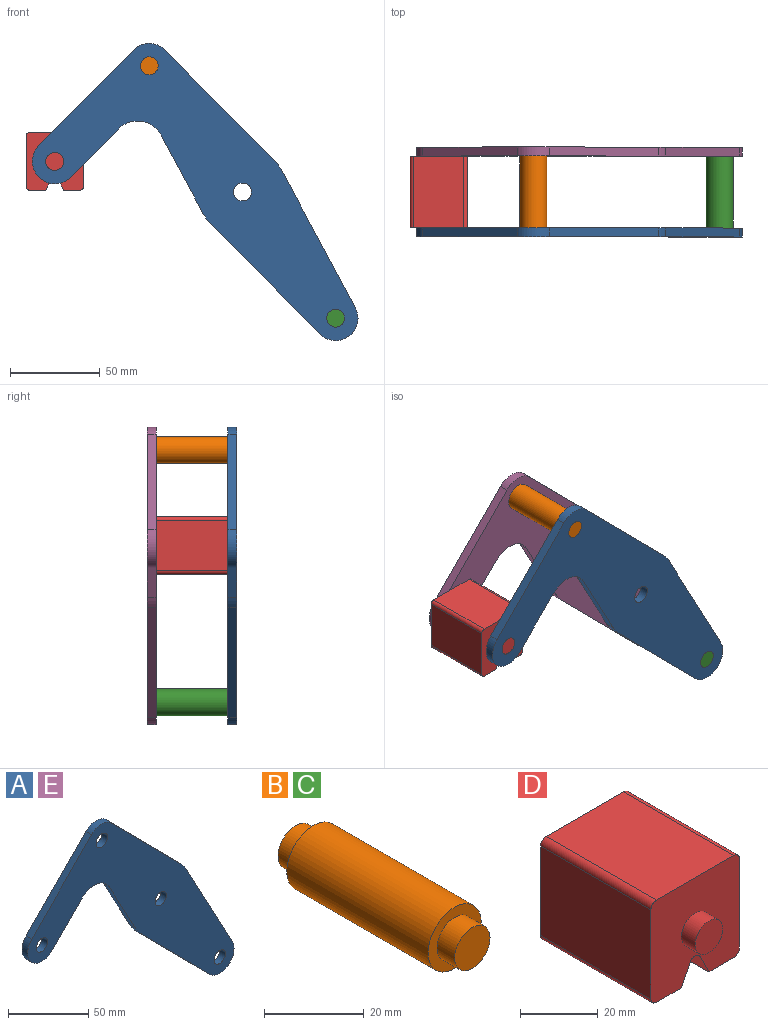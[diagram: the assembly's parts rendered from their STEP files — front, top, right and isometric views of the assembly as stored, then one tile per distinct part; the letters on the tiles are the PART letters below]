
ASSEMBLY  parts=5 mates=4
PART A: 18 faces, bbox 181.7x5x165.8 mm
  f0: plane 43.49x23.35mm, normal (-0.88,0,-0.47), area 246.8mm2, adj f1,f14,f16,f17
  f1: cylinder r=25mm len=5.75mm, axis (0,1,0), area 35.8mm2, adj f0,f2,f16,f17
  f2: plane 61.6x60.87mm, normal (-0.71,0,-0.7), area 433mm2, adj f1,f3,f16,f17
  f3: cylinder r=12.5mm len=21.39mm, axis (0,1,0), area 178.4mm2, adj f2,f4,f16,f17
  f4: plane 76.3x40.96mm, normal (0.88,0,0.47), area 433mm2, adj f3,f5,f16,f17
  f5: cylinder r=25mm len=5.75mm, axis (0,1,0), area 35.8mm2, adj f4,f6,f16,f17
  f6: plane 61.6x60.87mm, normal (0.71,0,0.7), area 433mm2, adj f5,f7,f16,f17
  f7: cylinder r=12.5mm len=17.78mm, axis (0,1,0), area 98.9mm2, adj f6,f8,f16,f17
  f8: plane 53.35x52.71mm, normal (-0.71,0,0.7), area 375mm2, adj f7,f9,f16,f17
  f9: cylinder r=12.5mm len=21.39mm, axis (0,1,0), area 196.3mm2, adj f8,f10,f16,f17
  f10: plane 26.86x26.54mm, normal (0.71,0,-0.7), area 188.8mm2, adj f9,f14,f16,f17
  f11: cylinder r=5mm len=10mm, axis (0,1,0), area 157.1mm2, adj f16,f17
  f12: cylinder r=5mm len=10mm, axis (0,1,0), area 157.1mm2, adj f16,f17
  f13: cylinder r=5mm len=10mm, axis (0,1,0), area 157.1mm2, adj f16,f17
  f14: cylinder r=15mm len=23.89mm, axis (0,1,0), area 140.2mm2, adj f0,f10,f16,f17
  f15: cylinder r=5mm len=10mm, axis (0,1,0), area 157.1mm2, adj f16,f17
  f16: plane 181.66x165.78mm, normal (0,-1,0), area 8710.1mm2, adj f0,f1,f2,f3,f4,f5,f6,f7
  f17: plane 181.66x165.78mm, normal (0,1,0), area 8710.1mm2, adj f0,f1,f2,f3,f4,f5,f6,f7
PART B: 7 faces, bbox 15x50x15 mm
  f0: cylinder r=7.5mm len=40mm, axis (0,-1,0), area 1885mm2, adj f2,f5
  f1: cylinder r=5mm len=10mm, axis (0,1,0), area 157.1mm2, adj f2,f3
  f2: plane 15x15mm, normal (0,-1,0), area 98.2mm2, adj f0,f1
  f3: plane 10x10mm, normal (0,-1,0), area 78.5mm2, adj f1
  f4: cylinder r=5mm len=10mm, axis (0,-1,0), area 157.1mm2, adj f5,f6
  f5: plane 15x15mm, normal (0,1,0), area 98.2mm2, adj f0,f4
  f6: plane 10x10mm, normal (0,1,0), area 78.5mm2, adj f4
PART C: same geometry as B
PART D: 18 faces, bbox 32.1x50x32.1 mm
  f0: plane 40x28.08mm, normal (1,0,0), area 1123.1mm2, adj f4,f10,f13,f14
  f1: plane 40x9.04mm, normal (0,0,-1), area 361.6mm2, adj f2,f4,f10,f14
  f2: plane 40x6.42mm, normal (-0.89,0,-0.45), area 287.2mm2, adj f1,f4,f10,f15
  f3: plane 40x6.42mm, normal (0.89,0,-0.45), area 287.2mm2, adj f4,f5,f10,f15
  f4: plane 32.08x32.08mm, normal (0,-1,0), area 900.6mm2, adj f0,f1,f2,f3,f5,f6,f7,f9
  f5: plane 40x9.04mm, normal (0,0,-1), area 361.6mm2, adj f3,f4,f10,f16
  f6: plane 40x28.08mm, normal (0,0,1), area 1123.1mm2, adj f4,f10,f13,f17
  f7: plane 40x28.08mm, normal (-1,0,0), area 1123.1mm2, adj f4,f10,f16,f17
  f8: plane 10x10mm, normal (0,-1,0), area 78.5mm2, adj f9
  f9: cylinder r=5mm len=10mm, axis (0,1,0), area 157.1mm2, adj f4,f8
  f10: plane 32.08x32.08mm, normal (0,1,0), area 900.6mm2, adj f0,f1,f2,f3,f5,f6,f7,f12
  f11: plane 10x10mm, normal (0,1,0), area 78.5mm2, adj f12
  f12: cylinder r=5mm len=10mm, axis (0,-1,0), area 157.1mm2, adj f10,f11
  f13: cylinder r=2mm len=40mm, axis (0,1,0), area 125.7mm2, adj f0,f4,f6,f10
  f14: cylinder r=2mm len=40mm, axis (0,-1,0), area 125.7mm2, adj f0,f1,f4,f10
  f15: cylinder r=2mm len=40mm, axis (0,1,0), area 177.1mm2, adj f2,f3,f4,f10
  f16: cylinder r=2mm len=40mm, axis (0,1,0), area 125.7mm2, adj f4,f5,f7,f10
  f17: cylinder r=2mm len=40mm, axis (0,-1,0), area 125.7mm2, adj f4,f6,f7,f10
PART E: same geometry as A
PLACE A t=(0,-20,0)mm fixed
PLACE B t=(0,-20,0)mm
PLACE C t=(103.95,-20,-140.78)mm
PLACE D t=(0,-20,0)mm
PLACE E t=(0,25,0)mm
MATE revolute A.f9 <-> D.f9  axis (0,1,0) through (-104.69,-20,17.04)mm
MATE fastened C.f0 <-> E.f3  axis (0,1,0) through (51.98,25,-70.39)mm
MATE fastened C.f0 <-> A.f3  axis (0,-1,0) through (51.98,-20,-70.39)mm
MATE revolute E.f7 <-> B.f0  axis (0,-1,0) through (-51.98,20,70.39)mm
